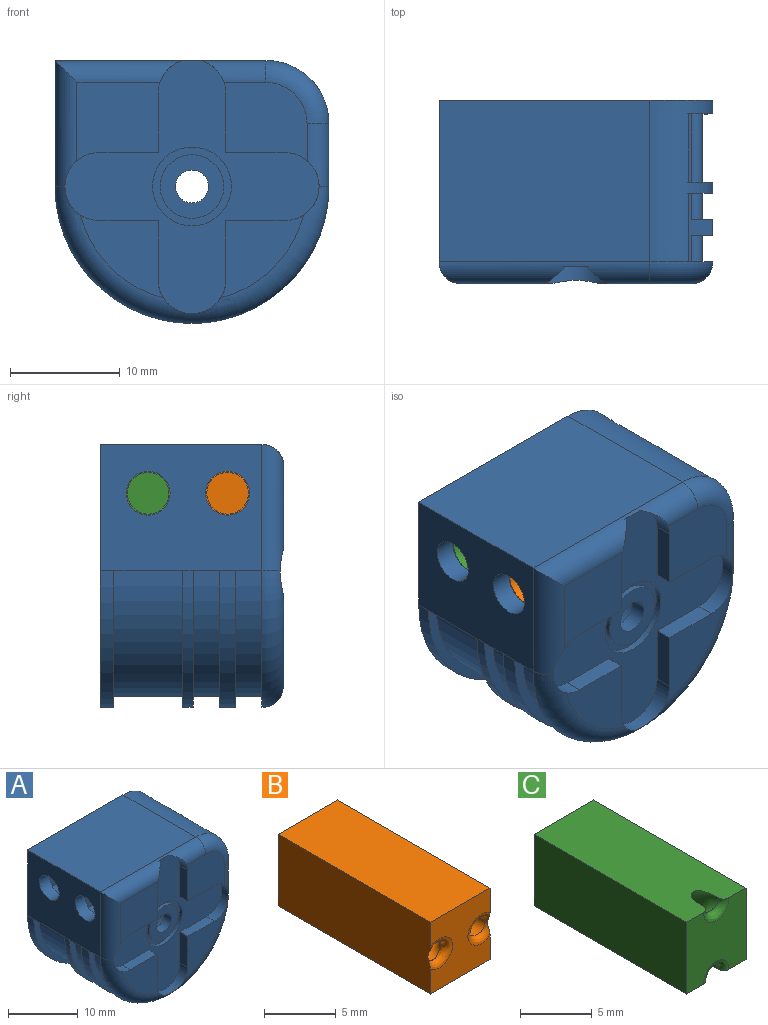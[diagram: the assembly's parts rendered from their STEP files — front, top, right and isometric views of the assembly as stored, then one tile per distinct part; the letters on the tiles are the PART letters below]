
ASSEMBLY  parts=3 mates=2
PART A: 70 faces, bbox 27.1x16.8x25.5 mm
  f0: plane 7.57x7.13mm, normal (0,-1,0), area 47.9mm2, adj f41,f43,f44,f45,f46,f68,f69
  f1: plane 7.56x7.56mm, normal (0,-1,0), area 32.5mm2, adj f46,f47,f48,f49,f50,f67
  f2: plane 7.56x7.56mm, normal (0,-1,0), area 32.5mm2, adj f50,f51,f52,f53,f54,f67
  f3: cylinder r=3mm len=13.55mm, axis (0,1,0), area 255.4mm2, adj f34,f59
  f4: plane 19.25x14.75mm, normal (0,0,1), area 283.9mm2, adj f13,f14,f34,f68
  f5: plane 7.57x7.13mm, normal (0,-1,0), area 44.9mm2, adj f40,f54,f55,f56,f57,f65,f66,f68
  f6: cylinder r=3.6mm len=7.2mm, axis (0,-1,0), area 13.6mm2, adj f39,f42
  f7: plane 3.8x1.5mm, normal (1,0,0), area 5.7mm2, adj f8,f15,f31,f36
  f8: cylinder r=12.5mm len=25mm, axis (0,1,0), area 58.9mm2, adj f7,f14,f31,f36
  f9: plane 5.75x1mm, normal (1,0,0), area 5.8mm2, adj f10,f13,f18,f22
  f10: cylinder r=12.5mm len=25mm, axis (0,1,0), area 39.3mm2, adj f9,f14,f18,f22
  f11: cylinder r=12.5mm len=25mm, axis (0,1,0), area 49.1mm2, adj f12,f14,f21,f34
  f12: plane 5.75x1.25mm, normal (1,0,0), area 7.2mm2, adj f11,f13,f21,f34
  f13: cylinder r=5.75mm len=14.75mm, axis (0,1,0), area 67.6mm2, adj f4,f9,f12,f17,f18,f21,f22,f23
  f14: plane 14.75x11.5mm, normal (-1,0,0), area 144.5mm2, adj f4,f8,f10,f11,f25,f26,f29,f33
  f15: plane 23x6.25mm, normal (0,0,1), area 134.2mm2, adj f7,f16,f18,f19,f31,f36,f62,f63
  f16: plane 25x22.8mm, normal (0,1,0), area 188.1mm2, adj f15,f17,f19,f35,f37,f38,f62,f65
  f17: plane 20.77x6.25mm, normal (0,0,-1), area 129.8mm2, adj f13,f16,f18,f19
  f18: plane 25x22.8mm, normal (0,-1,0), area 188.1mm2, adj f9,f10,f13,f15,f17,f19,f30,f32
  f19: plane 6.5x6.25mm, normal (1,0,0), area 28.1mm2, adj f15,f16,f17,f18,f26
  f20: plane 21x6.25mm, normal (0,0,1), area 131.2mm2, adj f21,f22,f24,f64
  f21: plane 25x22.8mm, normal (0,-1,0), area 188.1mm2, adj f11,f12,f13,f20,f23,f24,f27,f28
  f22: plane 25x22.8mm, normal (0,1,0), area 188.1mm2, adj f9,f10,f13,f20,f23,f24,f27,f28
  f23: plane 20.77x6.25mm, normal (0,0,-1), area 129.8mm2, adj f13,f21,f22,f24
  f24: plane 6.5x6.25mm, normal (1,0,0), area 28.1mm2, adj f20,f21,f22,f23,f25
  f25: cylinder r=2mm len=4mm, axis (-1,0,0), area 25.1mm2, adj f14,f24
  f26: cylinder r=2mm len=4mm, axis (-1,0,0), area 25.1mm2, adj f14,f19
  f27: plane 6.25x2.8mm, normal (1,0,0), area 17.5mm2, adj f21,f22,f28,f64
  f28: cylinder r=11.5mm len=23mm, axis (0,1,0), area 225.8mm2, adj f21,f22,f27,f29
  f29: plane 6.25x1mm, normal (0,0,-1), area 6.3mm2, adj f14,f21,f22,f28
  f30: plane 2.8x2.38mm, normal (1,0,0), area 6.7mm2, adj f18,f31,f32,f63
  f31: plane 25x16.3mm, normal (0,1,0), area 41.7mm2, adj f7,f8,f15,f30,f32,f33,f63
  f32: cylinder r=11.5mm len=23mm, axis (0,1,0), area 85.8mm2, adj f18,f30,f31,f33
  f33: plane 2.38x1mm, normal (0,0,-1), area 2.4mm2, adj f14,f18,f31,f32
  f34: plane 25x24mm, normal (0,1,0), area 497.6mm2, adj f3,f4,f11,f12,f13,f14
  f35: plane 2.8x2.38mm, normal (1,0,0), area 6.7mm2, adj f16,f36,f37,f62
  f36: plane 25x16.3mm, normal (0,-1,0), area 41.7mm2, adj f7,f8,f15,f35,f37,f38,f62
  f37: cylinder r=11.5mm len=23mm, axis (0,1,0), area 85.8mm2, adj f16,f35,f36,f38
  f38: plane 2.38x1mm, normal (0,0,-1), area 2.4mm2, adj f14,f16,f36,f37
  f39: plane 7.2x7.2mm, normal (0,-1,0), area 14.3mm2, adj f6,f60
  f40: cylinder r=3.1mm len=2.96mm, axis (0,-1,0), area 4.7mm2, adj f5,f42,f57,f68
  f41: cylinder r=3.1mm len=2.96mm, axis (0,-1,0), area 4.7mm2, adj f0,f42,f43,f68
  f42: plane 23.2x23.06mm, normal (0,-1,0), area 191.9mm2, adj f6,f40,f41,f43,f44,f45,f46,f47
  f43: plane 5.38x1.6mm, normal (1,0,0), area 8.6mm2, adj f0,f41,f42,f44
  f44: plane 1.6x0.02mm, normal (0.71,0,-0.71), area 0.1mm2, adj f0,f42,f43,f45
  f45: plane 5.38x1.6mm, normal (0,0,-1), area 8.6mm2, adj f0,f42,f44,f46
  f46: cylinder r=3.1mm len=6.2mm, axis (0,-1,0), area 14.6mm2, adj f0,f1,f42,f45,f47,f67,f69
  f47: plane 5.38x1.6mm, normal (0,0,1), area 8.6mm2, adj f1,f42,f46,f48
  f48: plane 1.6x0.02mm, normal (0.71,0,0.71), area 0.1mm2, adj f1,f42,f47,f49
  f49: plane 5.38x1.6mm, normal (1,0,0), area 8.6mm2, adj f1,f42,f48,f50
  f50: cylinder r=3.1mm len=6.2mm, axis (0,-1,0), area 14.5mm2, adj f1,f2,f42,f49,f51,f67
  f51: plane 5.38x1.6mm, normal (-1,0,0), area 8.6mm2, adj f2,f42,f50,f52
  f52: plane 1.6x0.02mm, normal (-0.71,0,0.71), area 0mm2, adj f2,f42,f51,f53
  f53: plane 5.38x1.6mm, normal (0,0,1), area 8.6mm2, adj f2,f42,f52,f54
  f54: cylinder r=3.1mm len=6.2mm, axis (0,-1,0), area 14.6mm2, adj f2,f5,f42,f53,f55,f65,f67
  f55: plane 5.38x1.6mm, normal (0,0,-1), area 8.6mm2, adj f5,f42,f54,f56
  f56: cylinder r=4.5mm len=1.6mm, axis (0,-1,0), area 0mm2, adj f5,f42,f55,f57
  f57: plane 5.38x1.6mm, normal (-1,0,0), area 8.6mm2, adj f5,f40,f42,f56
  f58: cylinder r=1.5mm len=3mm, axis (0,-1,0), area 14.1mm2, adj f59,f61
  f59: plane 6x6mm, normal (0,1,0), area 21.2mm2, adj f3,f58
  f60: cylinder r=2.9mm len=5.8mm, axis (0,1,0), area 9.1mm2, adj f39,f61
  f61: plane 5.8x5.8mm, normal (0,-1,0), area 19.4mm2, adj f58,f60
  f62: cylinder r=1mm len=2.38mm, axis (0,1,0), area 3.7mm2, adj f15,f16,f35,f36
  f63: cylinder r=1mm len=2.38mm, axis (0,1,0), area 3.7mm2, adj f15,f18,f30,f31
  f64: cylinder r=1mm len=6.25mm, axis (0,1,0), area 9.8mm2, adj f20,f21,f22,f27
  f65: cylinder r=2mm len=5.75mm, axis (0,0,-1), area 16.2mm2, adj f5,f16,f54,f66,f67
  f66: torus R=3.75mm, axis (0,-1,0), area 24.8mm2, adj f5,f13,f16,f65,f68
  f67: torus R=10.5mm, axis (0,-1,0), area 107.6mm2, adj f1,f2,f16,f46,f50,f54,f65,f69
  f68: cylinder r=2mm len=19.25mm, axis (1,0,0), area 47mm2, adj f0,f4,f5,f40,f41,f42,f66,f69
  f69: cylinder r=2mm len=11.5mm, axis (0,0,1), area 32mm2, adj f0,f14,f46,f67,f68
PART B: 11 faces, bbox 6.7x15x6.1 mm
  f0: plane 15x5.85mm, normal (0,0,-1), area 87.8mm2, adj f1,f3,f4,f7
  f1: plane 15x6.1mm, normal (1,0,0), area 91.3mm2, adj f0,f2,f4,f7,f10
  f2: plane 15x5.85mm, normal (0,0,1), area 87.8mm2, adj f1,f3,f4,f7
  f3: plane 15x6.1mm, normal (-1,0,0), area 91.3mm2, adj f0,f2,f4,f7,f9
  f4: plane 6.1x5.85mm, normal (0,1,0), area 24.3mm2, adj f0,f1,f2,f3,f5
  f5: cylinder r=1.9mm len=9mm, axis (0,1,0), area 107.4mm2, adj f4,f6
  f6: plane 3.8x3.8mm, normal (0,1,0), area 11.3mm2, adj f5
  f7: plane 6.1x5.85mm, normal (0,-1,0), area 26.6mm2, adj f0,f1,f2,f3,f9,f10
  f8: torus R=2.15mm, axis (0,0,1), area 26.6mm2, adj f9,f10
  f9: bspline ~2.61x2.5mm, area 4.7mm2, adj f3,f7,f8
  f10: bspline ~2.62x2.5mm, area 4.3mm2, adj f1,f7,f8
PART C: 11 faces, bbox 5.9x15x8.1 mm
  f0: plane 15.02x5.87mm, normal (0,0,-1), area 84.7mm2, adj f1,f3,f4,f7,f8,f10
  f1: plane 15x6.1mm, normal (1,0,0), area 91.5mm2, adj f0,f2,f4,f7
  f2: plane 15.02x5.87mm, normal (0,0,1), area 84.7mm2, adj f1,f3,f4,f7,f8,f9
  f3: plane 15x6.1mm, normal (-1,0,0), area 91.5mm2, adj f0,f2,f4,f7
  f4: plane 6.1x5.85mm, normal (0,1,0), area 24.3mm2, adj f0,f1,f2,f3,f5
  f5: cylinder r=1.9mm len=9mm, axis (0,1,0), area 107.4mm2, adj f4,f6
  f6: plane 3.8x3.8mm, normal (0,1,0), area 11.3mm2, adj f5
  f7: plane 6.1x5.85mm, normal (0,-1,0), area 30.5mm2, adj f0,f1,f2,f3,f9,f10
  f8: torus R=3.05mm, axis (1,0,0), area 33.9mm2, adj f0,f2,f9,f10
  f9: bspline ~2.5x1.5mm, area 2.6mm2, adj f2,f7,f8
  f10: bspline ~2.5x1.5mm, area 2.6mm2, adj f0,f7,f8
PLACE A at identity
PLACE B rot(axis=(-0.71,0.71,0),180deg) t=(-10.5,-11.63,7.05)mm
PLACE C rot(axis=(0,0,1),90deg) t=(-10.5,-4.37,7.05)mm
MATE slider B.f5 <-> A.f26  axis (-1,0,0) through (-10.5,-11.63,7.05)mm
MATE slider C.f5 <-> A.f25  axis (-1,0,0) through (-10.5,-4.37,7.05)mm
